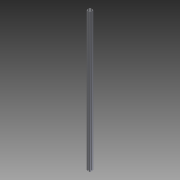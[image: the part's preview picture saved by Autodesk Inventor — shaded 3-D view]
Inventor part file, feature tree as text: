
AUTODESK INVENTOR PART (.ipt)
format: ipt  version: 2016 (Build 200138000, 138)  size: 213,504 bytes
history: native  units: mm
features: other x42, sketch x5, hole x4, extrude x1
ambient origin geometry x8: Origin, YZ Plane, XZ Plane, XY Plane, X Axis, Y Axis, Z Axis, Center Point
bodies: Solid1 (feature_tree)
feature tree (52):
  extrude  "Extrusion1"  [1 undecoded]
  hole  "Drilling 1"  [1 undecoded]
  hole  "Drilling 2"  [1 undecoded]
  hole  "Drilling 3"  [1 undecoded]
  hole  "Drilling 4"  [1 undecoded]
  other  "side_4d_XY"
  other  "side_4d_YZ"
  other  "side_4d_ZX"
  other  "side_4d_X"
  other  "side_4d_Y"
  other  "side_4d_Z"
  other  "side_4d_Center"
  other  "side_1a_XY"
  other  "side_1a_YZ"
  other  "side_1a_ZX"
  other  "side_1a_X"
  other  "side_1a_Y"
  other  "side_1a_Z"
  other  "side_1a_Center"
  other  "side_2b_XY"
  other  "side_2b_YZ"
  other  "side_2b_ZX"
  other  "side_2b_X"
  other  "side_2b_Y"
  other  "side_2b_Z"
  other  "side_2b_Center"
  other  "side_3c_XY"
  other  "side_3c_YZ"
  other  "side_3c_ZX"
  other  "side_3c_X"
  other  "side_3c_Y"
  other  "side_3c_Z"
  other  "side_3c_Center"
  other  "end_XY"
  other  "end_YZ"
  other  "end_ZX"
  other  "end_X"
  other  "end_Y"
  other  "end_Z"
  other  "end_Center"
  other  "start_XY"
  other  "start_YZ"
  other  "start_ZX"
  other  "start_X"
  other  "start_Y"
  other  "start_Z"
  other  "start_Center"
  sketch  "Skizze_1"  dims[d0=1627.0mm d1=0.0mm]
  sketch  "Sketch2"  dims[d2=5.0mm d3=6.0mm d4=4.0mm d5=2.0mm d6=90.0deg d7=6000.0mm d8=0.0mm]
  sketch  "Sketch3"  dims[d9=5.0mm d10=6.0mm d11=4.0mm d12=2.0mm d13=90.0deg d14=6000.0mm d15=0.0mm]
  sketch  "Sketch4"  dims[d16=5.0mm d17=6.0mm d18=4.0mm d19=2.0mm d20=90.0deg d21=6000.0mm d22=0.0mm]
  sketch  "Sketch5"  dims[d23=5.0mm d24=6.0mm d25=4.0mm d26=2.0mm d27=90.0deg d28=6000.0mm d29=0.0mm]
note: 5 required parameter values undecoded (feature->parameter linkage not recoverable at this tier; creation-order binding heuristic only, values carry confidence <= 0.55)
